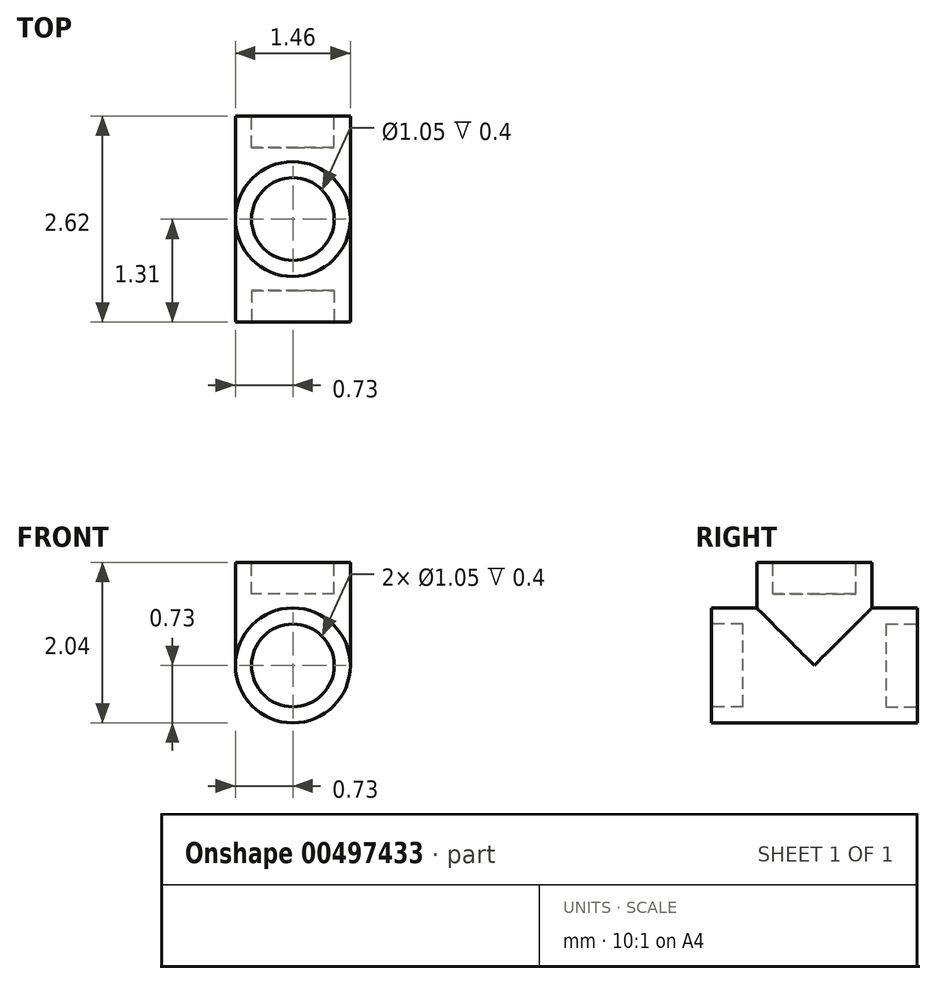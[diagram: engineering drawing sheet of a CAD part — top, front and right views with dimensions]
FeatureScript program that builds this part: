
annotation { "Feature Type Name" : "Feature", "Feature Type Description" : "" }
export const myFeature = defineFeature(function(context is Context, id is Id, definition is map)
    precondition{}
    {
        {
            var Q0;
            Q0=qCreatedBy(makeId("Front.planeOp"),FACE);
            var sketch = newSketch(context, id + "F0", { "sketchPlane" : qUnion([Q0])});
            skCircle(sketch, "E0", {"center": v(0, 0) * mm, "radius": 0.73 * mm});
            skSolve(sketch);
        }
        {
            var Q0;
            Q0=qSketchRegion(id+"F0",true);
            extrude(context, id + "F1", {"entities" : qUnion([Q0]), "depth" : 2.62 * mm});
        }
        {
            var Q0;
            Q0=qCreatedBy(makeId("Top.planeOp"),FACE);
            var sketch = newSketch(context, id + "F2", { "sketchPlane" : qUnion([Q0])});
            skLineSegment(sketch, "E1", {"start": v(0, 0) * mm, "end": v(0, -1.31) * mm});
            skCircle(sketch, "E2", {"center": v(0, -1.31) * mm, "radius": 0.73 * mm});
            skSolve(sketch);
        }
        {
            var Q0;
            Q0=qSketchRegion(id+"F2",true);
            extrude(context, id + "F3", {"entities" : qUnion([Q0]), "operationType" : NewBodyOperationType.ADD, "depth" : 1.31 * mm});
        }
        {
            var Q0;
            Q0=makeQuery(id+"F1.opExtrude","CAP_FACE",FACE,{"disambiguationData":[OSD([sQuery(id+"F0.wireOp",EDGE,"E0")])],"isStart":true});
            var sketch = newSketch(context, id + "F4", { "sketchPlane" : qUnion([Q0])});
            skCircle(sketch, "E3", {"center": v(0, 0) * mm, "radius": 0.53 * mm});
            skSolve(sketch);
        }
        {
            var Q0;
            Q0=qSketchRegion(id+"F4",true);
            extrude(context, id + "F5", {"entities" : qUnion([Q0]), "operationType" : NewBodyOperationType.REMOVE, "oppositeDirection" : true, "depth" : .4 * mm});
        }
        {
            var Q0;
            Q0=makeQuery(id+"F3.opExtrude","CAP_FACE",FACE,{"disambiguationData":[OSD([sQuery(id+"F2.wireOp",EDGE,"E2")])],"isStart":false});
            var sketch = newSketch(context, id + "F6", { "sketchPlane" : qUnion([Q0])});
            skCircle(sketch, "E4", {"center": v(0, -1.31) * mm, "radius": 0.53 * mm});
            skSolve(sketch);
        }
        {
            var Q0;
            Q0=qSketchRegion(id+"F6",true);
            extrude(context, id + "F7", {"entities" : qUnion([Q0]), "operationType" : NewBodyOperationType.REMOVE, "oppositeDirection" : true, "depth" : .4 * mm, "hasSecondDirection" : true, "secondDirectionOppositeDirection" : false, "secondDirectionDepth" : .4 * mm});
        }
        {
            var Q0;
            Q0=makeQuery(id+"F1.opExtrude","CAP_FACE",FACE,{"disambiguationData":[OSD([sQuery(id+"F0.wireOp",EDGE,"E0")])],"isStart":false});
            var sketch = newSketch(context, id + "F8", { "sketchPlane" : qUnion([Q0])});
            skCircle(sketch, "E5", {"center": v(0, 0) * mm, "radius": 0.53 * mm});
            skSolve(sketch);
        }
        {
            var Q0;
            Q0=qSketchRegion(id+"F8",true);
            extrude(context, id + "F9", {"entities" : qUnion([Q0]), "operationType" : NewBodyOperationType.REMOVE, "oppositeDirection" : true, "depth" : .4 * mm});
        }
    });
